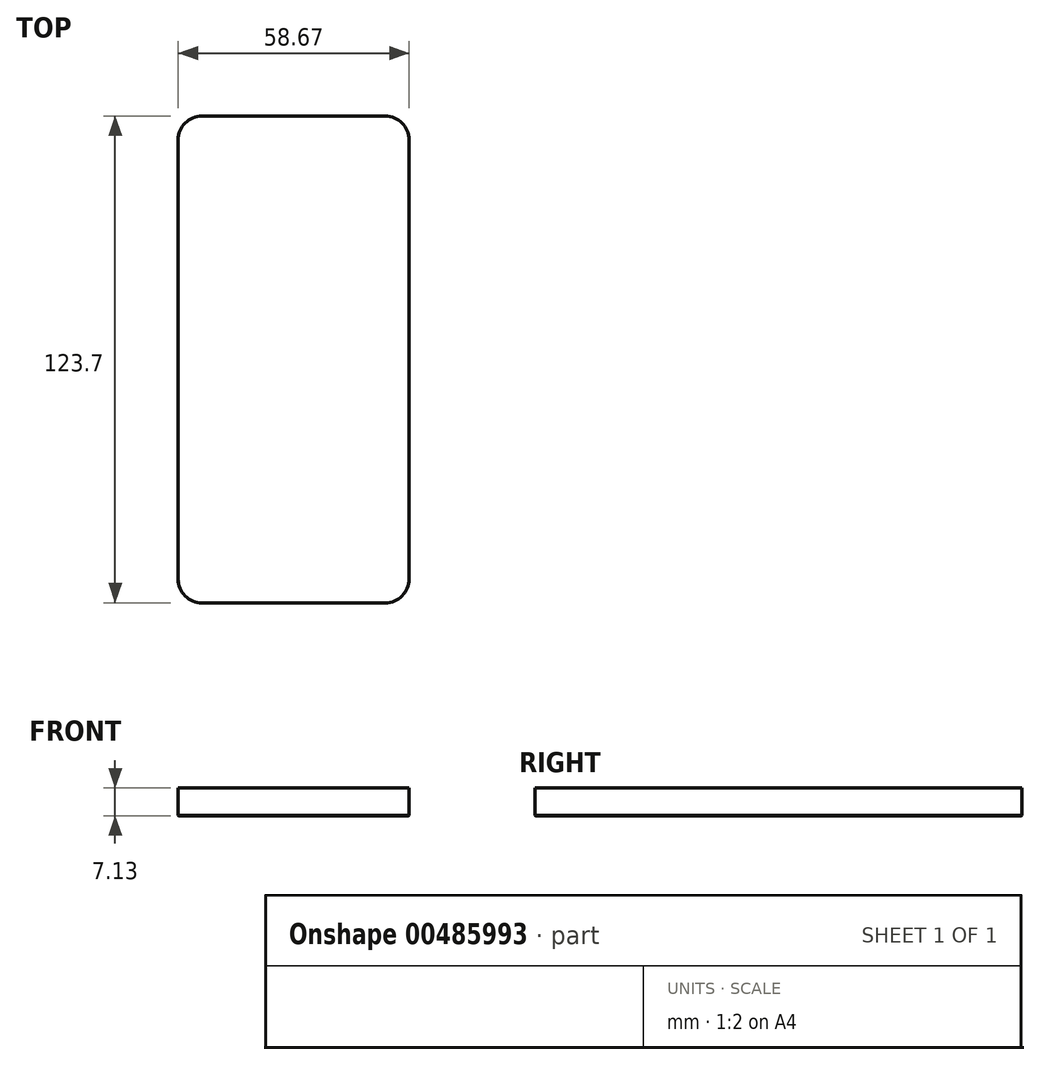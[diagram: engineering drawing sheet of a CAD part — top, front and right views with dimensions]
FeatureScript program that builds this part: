
annotation { "Feature Type Name" : "Feature", "Feature Type Description" : "" }
export const myFeature = defineFeature(function(context is Context, id is Id, definition is map)
    precondition{}
    {
        {
            var Q0;
            Q0=qCreatedBy(makeId("Top.planeOp"),FACE);
            var sketch = newSketch(context, id + "F0", { "sketchPlane" : qUnion([Q0])});
            skLineSegment(sketch, "E0.bottom", {"start": v(-6.07, 0) * mm, "end": v(-52.6, 0) * mm});
            skLineSegment(sketch, "E0.top", {"start": v(-6.07, 123.7) * mm, "end": v(-52.6, 123.7) * mm});
            skLineSegment(sketch, "E0.left", {"start": v(0, 6.07) * mm, "end": v(0, 117.63) * mm});
            skLineSegment(sketch, "E0.right", {"start": v(-58.67, 6.07) * mm, "end": v(-58.67, 117.63) * mm});
            skPoint(sketch, "E1.visualSharp", {"position": v(-58.67, 123.7) * mm});
            skArc(sketch, "E1.filletArc", {"start": v(-52.6, 123.7) * mm, "mid": v(-56.9, 121.92) * mm, "end": v(-58.67, 117.63) * mm});
            skPoint(sketch, "E2.visualSharp", {"position": v(0, 123.7) * mm});
            skArc(sketch, "E2.filletArc", {"start": v(0, 117.63) * mm, "mid": v(-1.78, 121.92) * mm, "end": v(-6.07, 123.7) * mm});
            skPoint(sketch, "E3.visualSharp", {"position": v(0, 0) * mm});
            skArc(sketch, "E3.filletArc", {"start": v(-6.07, 0) * mm, "mid": v(-1.78, 1.78) * mm, "end": v(0, 6.07) * mm});
            skPoint(sketch, "E4.visualSharp", {"position": v(-58.67, 0) * mm});
            skArc(sketch, "E4.filletArc", {"start": v(-58.67, 6.07) * mm, "mid": v(-56.9, 1.78) * mm, "end": v(-52.6, 0) * mm});
            skSolve(sketch);
        }
        {
            var Q0;
            Q0=makeQuery(id+"F0.imprint","IMPRINT",FACE,{"disambiguationData":[TD([[makeQuery(id+"F0.imprint","IMPRINT",EDGE,{"derivedFrom":sQuery(id+"F0.wireOp",EDGE,"E0.bottom")}),-1.0]])]});
            extrude(context, id + "F1", {"entities" : qUnion([Q0]), "depth" : 7.13 * mm});
        }
        {
            var Q0;
            Q0=makeQuery(id+"F1.opExtrude","CAP_EDGE",EDGE,{"disambiguationData":[OSD([sQuery(id+"F0.wireOp",EDGE,"E0.right")])],"isStart":true});
            var Q1;
            Q1=makeQuery(id+"F1.opExtrude","CAP_EDGE",EDGE,{"disambiguationData":[OSD([sQuery(id+"F0.wireOp",EDGE,"E4.filletArc")])],"isStart":true});
            var Q2;
            Q2=makeQuery(id+"F1.opExtrude","CAP_EDGE",EDGE,{"disambiguationData":[OSD([sQuery(id+"F0.wireOp",EDGE,"E0.bottom")])],"isStart":true});
            var Q3;
            Q3=makeQuery(id+"F1.opExtrude","CAP_EDGE",EDGE,{"disambiguationData":[OSD([sQuery(id+"F0.wireOp",EDGE,"E0.left")])],"isStart":true});
            var Q4;
            Q4=makeQuery(id+"F1.opExtrude","CAP_EDGE",EDGE,{"disambiguationData":[OSD([sQuery(id+"F0.wireOp",EDGE,"E2.filletArc")])],"isStart":true});
            var Q5;
            Q5=makeQuery(id+"F1.opExtrude","CAP_EDGE",EDGE,{"disambiguationData":[OSD([sQuery(id+"F0.wireOp",EDGE,"E0.top")])],"isStart":true});
            var Q6;
            Q6=makeQuery(id+"F1.opExtrude","CAP_EDGE",EDGE,{"disambiguationData":[OSD([sQuery(id+"F0.wireOp",EDGE,"E1.filletArc")])],"isStart":true});
            var Q7;
            Q7=makeQuery(id+"F1.opExtrude","CAP_EDGE",EDGE,{"disambiguationData":[OSD([sQuery(id+"F0.wireOp",EDGE,"E3.filletArc")])],"isStart":true});
            chamfer(context, id + "F2", {"entities" : qUnion([Q0, Q1, Q2, Q3, Q4, Q5, Q6, Q7]), "width" : .14 * mm, "tangentPropagation" : true});
        }
        {
            var Q0;
            Q0=makeQuery(id+"F1.opExtrude","CAP_FACE",FACE,{"disambiguationData":[OSD([sQuery(id+"F0.wireOp",EDGE,"E0.bottom"),sQuery(id+"F0.wireOp",EDGE,"E0.top"),sQuery(id+"F0.wireOp",EDGE,"E0.left"),sQuery(id+"F0.wireOp",EDGE,"E0.right"),sQuery(id+"F0.wireOp",EDGE,"E1.filletArc"),sQuery(id+"F0.wireOp",EDGE,"E2.filletArc"),sQuery(id+"F0.wireOp",EDGE,"E3.filletArc"),sQuery(id+"F0.wireOp",EDGE,"E4.filletArc")])],"isStart":true});
            cPlane(context, id + "F3", {"entities" : qUnion([Q0]), "cplaneType" : CPlaneType.OFFSET, "offset" : 25.4 * mm, "width" : 152.4 * mm, "height" : 152.4 * mm});
        }
    });
